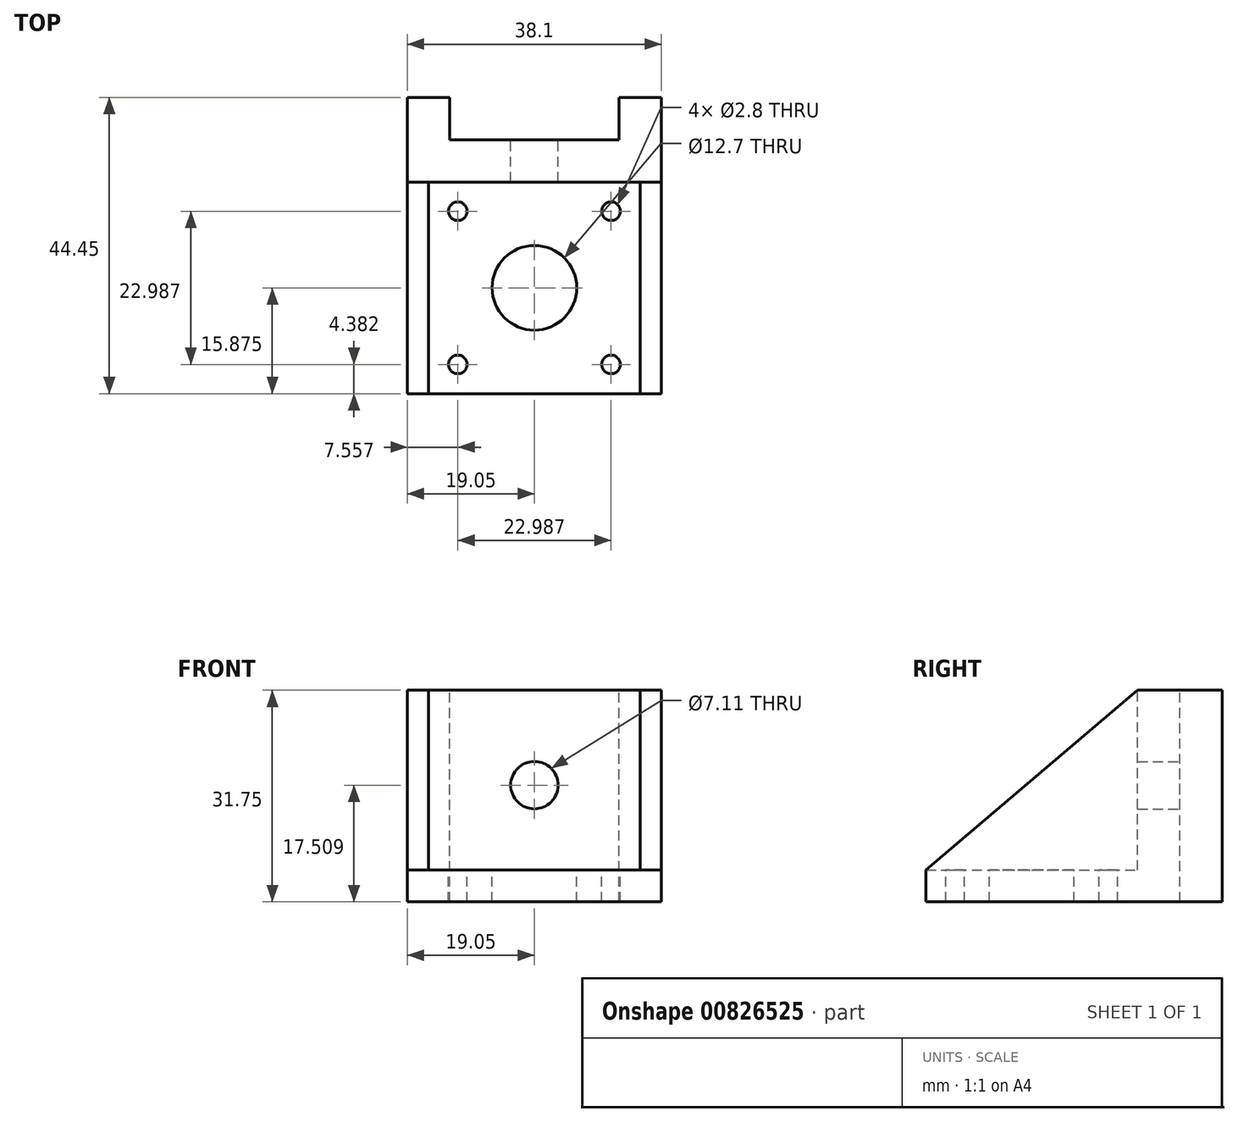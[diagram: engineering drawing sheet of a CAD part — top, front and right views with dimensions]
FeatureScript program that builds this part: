
annotation { "Feature Type Name" : "Feature", "Feature Type Description" : "" }
export const myFeature = defineFeature(function(context is Context, id is Id, definition is map)
    precondition{}
    {
        {
            var Q0;
            Q0=qCreatedBy(makeId("Front.planeOp"),FACE);
            var sketch = newSketch(context, id + "F0", { "sketchPlane" : qUnion([Q0])});
            skLineSegment(sketch, "E0.bottom", {"start": v(12.7, 0) * mm, "end": v(-12.7, 0) * mm});
            skLineSegment(sketch, "E0.top", {"start": v(12.7, 31.75) * mm, "end": v(-12.7, 31.75) * mm});
            skLineSegment(sketch, "E0.left", {"start": v(12.7, 0) * mm, "end": v(12.7, 31.75) * mm});
            skLineSegment(sketch, "E0.right", {"start": v(-12.7, 0) * mm, "end": v(-12.7, 31.75) * mm});
            skPoint(sketch, "E0.middle", {"position": v(0, 15.88) * mm});
            skSolve(sketch);
        }
        {
            var Q0;
            Q0 = qSketchRegion(id + "F0", true);
            extrude(context, id + "F1", {"entities" : qUnion([Q0]), "depth" : 6.35 * mm, "offsetDistance" : 25.4 * mm});
        }
        {
            var Q0;
            Q0=makeQuery(id+"F1.opExtrude","CAP_FACE",FACE,{"disambiguationData":[OSD([sQuery(id+"F0.wireOp",EDGE,"E0.bottom"),sQuery(id+"F0.wireOp",EDGE,"E0.top"),sQuery(id+"F0.wireOp",EDGE,"E0.left"),sQuery(id+"F0.wireOp",EDGE,"E0.right")])],"isStart":false});
            var sketch = newSketch(context, id + "F2", { "sketchPlane" : qUnion([Q0])});
            skLineSegment(sketch, "E1.bottom", {"start": v(-12.7, 0) * mm, "end": v(-19.05, 0) * mm});
            skLineSegment(sketch, "E1.top", {"start": v(-12.7, 31.75) * mm, "end": v(-19.05, 31.75) * mm});
            skLineSegment(sketch, "E1.left", {"start": v(-12.7, 0) * mm, "end": v(-12.7, 31.75) * mm});
            skLineSegment(sketch, "E1.right", {"start": v(-19.05, 0) * mm, "end": v(-19.05, 31.75) * mm});
            skLineSegment(sketch, "E2.bottom", {"start": v(12.7, 0) * mm, "end": v(19.05, 0) * mm});
            skLineSegment(sketch, "E2.top", {"start": v(12.7, 31.75) * mm, "end": v(19.05, 31.75) * mm});
            skLineSegment(sketch, "E2.left", {"start": v(12.7, 0) * mm, "end": v(12.7, 31.75) * mm});
            skLineSegment(sketch, "E2.right", {"start": v(19.05, 0) * mm, "end": v(19.05, 31.75) * mm});
            skSolve(sketch);
        }
        {
            var Q0;
            Q0 = qSketchRegion(id + "F2", true);
            extrude(context, id + "F3", {"entities" : qUnion([Q0]), "operationType" : NewBodyOperationType.ADD, "depth" : -12.7 * mm, "offsetDistance" : 25.4 * mm});
        }
        {
            var Q0;
            Q0=makeQuery(id+"F3.boolean.opBoolean","MERGE",FACE,{"derivedFrom":[makeQuery(id+"F1.opExtrude","CAP_FACE",FACE,{"disambiguationData":[OSD([sQuery(id+"F0.wireOp",EDGE,"E0.bottom"),sQuery(id+"F0.wireOp",EDGE,"E0.top"),sQuery(id+"F0.wireOp",EDGE,"E0.left"),sQuery(id+"F0.wireOp",EDGE,"E0.right")])],"isStart":false}),makeQuery(id+"F3.opExtrude","CAP_FACE",FACE,{"disambiguationData":[OSD([sQuery(id+"F2.wireOp",EDGE,"E1.bottom"),sQuery(id+"F2.wireOp",EDGE,"E1.top"),sQuery(id+"F2.wireOp",EDGE,"E1.left"),sQuery(id+"F2.wireOp",EDGE,"E1.right")])],"isStart":true}),makeQuery(id+"F3.opExtrude","CAP_FACE",FACE,{"disambiguationData":[OSD([sQuery(id+"F2.wireOp",EDGE,"E2.bottom"),sQuery(id+"F2.wireOp",EDGE,"E2.top"),sQuery(id+"F2.wireOp",EDGE,"E2.left"),sQuery(id+"F2.wireOp",EDGE,"E2.right")])],"isStart":true})]});
            var sketch = newSketch(context, id + "F4", { "sketchPlane" : qUnion([Q0])});
            skLineSegment(sketch, "E3.bottom", {"start": v(-19.05, 0) * mm, "end": v(19.05, 0) * mm});
            skLineSegment(sketch, "E3.top", {"start": v(-19.05, 4.76) * mm, "end": v(19.05, 4.76) * mm});
            skLineSegment(sketch, "E3.left", {"start": v(-19.05, 0) * mm, "end": v(-19.05, 4.76) * mm});
            skLineSegment(sketch, "E3.right", {"start": v(19.05, 0) * mm, "end": v(19.05, 4.76) * mm});
            skSolve(sketch);
        }
        {
            var Q0;
            Q0 = qSketchRegion(id + "F4", true);
            extrude(context, id + "F5", {"entities" : qUnion([Q0]), "operationType" : NewBodyOperationType.ADD, "depth" : 31.75 * mm, "offsetDistance" : 25.4 * mm});
        }
        {
            var Q0;
            Q0=makeQuery(id+"F5.boolean.opBoolean","MERGE",FACE,{"derivedFrom":[makeQuery(id+"F3.opExtrude","SWEPT_FACE",FACE,{"disambiguationData":[OSD([sQuery(id+"F2.wireOp",EDGE,"E1.right")])]}),makeQuery(id+"F5.opExtrude","SWEPT_FACE",FACE,{"disambiguationData":[OSD([sQuery(id+"F4.wireOp",EDGE,"E3.left")])]})]});
            var sketch = newSketch(context, id + "F6", { "sketchPlane" : qUnion([Q0])});
            skLineSegment(sketch, "E4", {"start": v(6.35, 31.75) * mm, "end": v(38.1, 4.76) * mm});
            skLineSegment(sketch, "E5", {"start": v(38.1, 4.76) * mm, "end": v(6.35, 4.76) * mm});
            skLineSegment(sketch, "E6", {"start": v(6.35, 4.76) * mm, "end": v(6.35, 31.75) * mm});
            skSolve(sketch);
        }
        {
            var Q0;
            Q0=makeQuery(id+"F6.imprint","IMPRINT",FACE,{"disambiguationData":[TD([[makeQuery(id+"F6.imprint","IMPRINT",EDGE,{"derivedFrom":sQuery(id+"F6.wireOp",EDGE,"E4")}),-1.0]])]});
            extrude(context, id + "F7", {"entities" : qUnion([Q0]), "operationType" : NewBodyOperationType.ADD, "depth" : -3.17 * mm, "offsetDistance" : 25.4 * mm});
        }
        {
            var Q0;
            Q0=makeQuery(id+"F5.boolean.opBoolean","MERGE",FACE,{"derivedFrom":[makeQuery(id+"F3.opExtrude","SWEPT_FACE",FACE,{"disambiguationData":[OSD([sQuery(id+"F2.wireOp",EDGE,"E2.right")])]}),makeQuery(id+"F5.opExtrude","SWEPT_FACE",FACE,{"disambiguationData":[OSD([sQuery(id+"F4.wireOp",EDGE,"E3.right")])]})]});
            var sketch = newSketch(context, id + "F8", { "sketchPlane" : qUnion([Q0])});
            skLineSegment(sketch, "E7", {"start": v(-6.35, 31.75) * mm, "end": v(-38.1, 4.76) * mm});
            skLineSegment(sketch, "E8", {"start": v(-38.1, 4.76) * mm, "end": v(-6.35, 4.76) * mm});
            skLineSegment(sketch, "E9", {"start": v(-6.35, 4.76) * mm, "end": v(-6.35, 31.75) * mm});
            skSolve(sketch);
        }
        {
            var Q0;
            Q0 = qSketchRegion(id + "F8", true);
            extrude(context, id + "F9", {"entities" : qUnion([Q0]), "operationType" : NewBodyOperationType.ADD, "depth" : -3.17 * mm, "offsetDistance" : 25.4 * mm});
        }
        {
            var Q0;
            Q0=qCreatedBy(makeId("Front.planeOp"),FACE);
            var sketch = newSketch(context, id + "F10", { "sketchPlane" : qUnion([Q0])});
            skCircle(sketch, "E10", {"center": v(0, 17.5) * mm, "radius": 3.56 * mm});
            skLineSegment(sketch, "E11", {"start": v(0, 31.84) * mm, "end": v(0, 3.18) * mm, "construction": true});
            skSolve(sketch);
        }
        {
            var Q0;
            Q0 = qSketchRegion(id + "F10", true);
            extrude(context, id + "F11", {"entities" : qUnion([Q0]), "operationType" : NewBodyOperationType.REMOVE, "oppositeDirection" : true, "depth" : -6.35 * mm, "offsetDistance" : 25.4 * mm});
        }
        {
            var Q0;
            Q0=makeQuery(id+"F5.opExtrude","SWEPT_FACE",FACE,{"disambiguationData":[OSD([sQuery(id+"F4.wireOp",EDGE,"E3.top")])]});
            var sketch = newSketch(context, id + "F12", { "sketchPlane" : qUnion([Q0])});
            skLineSegment(sketch, "E12.bottom", {"start": v(-11.5, -10.73) * mm, "end": v(11.5, -10.73) * mm, "construction": true});
            skLineSegment(sketch, "E12.top", {"start": v(-11.5, -33.72) * mm, "end": v(11.5, -33.72) * mm, "construction": true});
            skLineSegment(sketch, "E12.left", {"start": v(-11.5, -10.73) * mm, "end": v(-11.5, -33.72) * mm, "construction": true});
            skLineSegment(sketch, "E12.right", {"start": v(11.5, -10.73) * mm, "end": v(11.5, -33.72) * mm, "construction": true});
            skPoint(sketch, "E12.middle", {"position": v(0, -22.23) * mm});
            skCircle(sketch, "E13", {"center": v(11.5, -33.72) * mm, "radius": 1.4 * mm});
            skCircle(sketch, "E14", {"center": v(-11.5, -33.72) * mm, "radius": 1.4 * mm});
            skCircle(sketch, "E15", {"center": v(11.5, -10.73) * mm, "radius": 1.4 * mm});
            skCircle(sketch, "E16", {"center": v(-11.5, -10.73) * mm, "radius": 1.4 * mm});
            skLineSegment(sketch, "E17", {"start": v(0, -6.35) * mm, "end": v(0, -38.1) * mm, "construction": true});
            skCircle(sketch, "E18", {"center": v(0, -22.23) * mm, "radius": 6.35 * mm});
            skSolve(sketch);
        }
        {
            var Q0;
            Q0 = qSketchRegion(id + "F12", true);
            extrude(context, id + "F13", {"entities" : qUnion([Q0]), "operationType" : NewBodyOperationType.REMOVE, "endBound" : BoundingType.UP_TO_NEXT, "oppositeDirection" : true, "depth" : 25.4 * mm, "offsetDistance" : 25.4 * mm});
        }
    });
